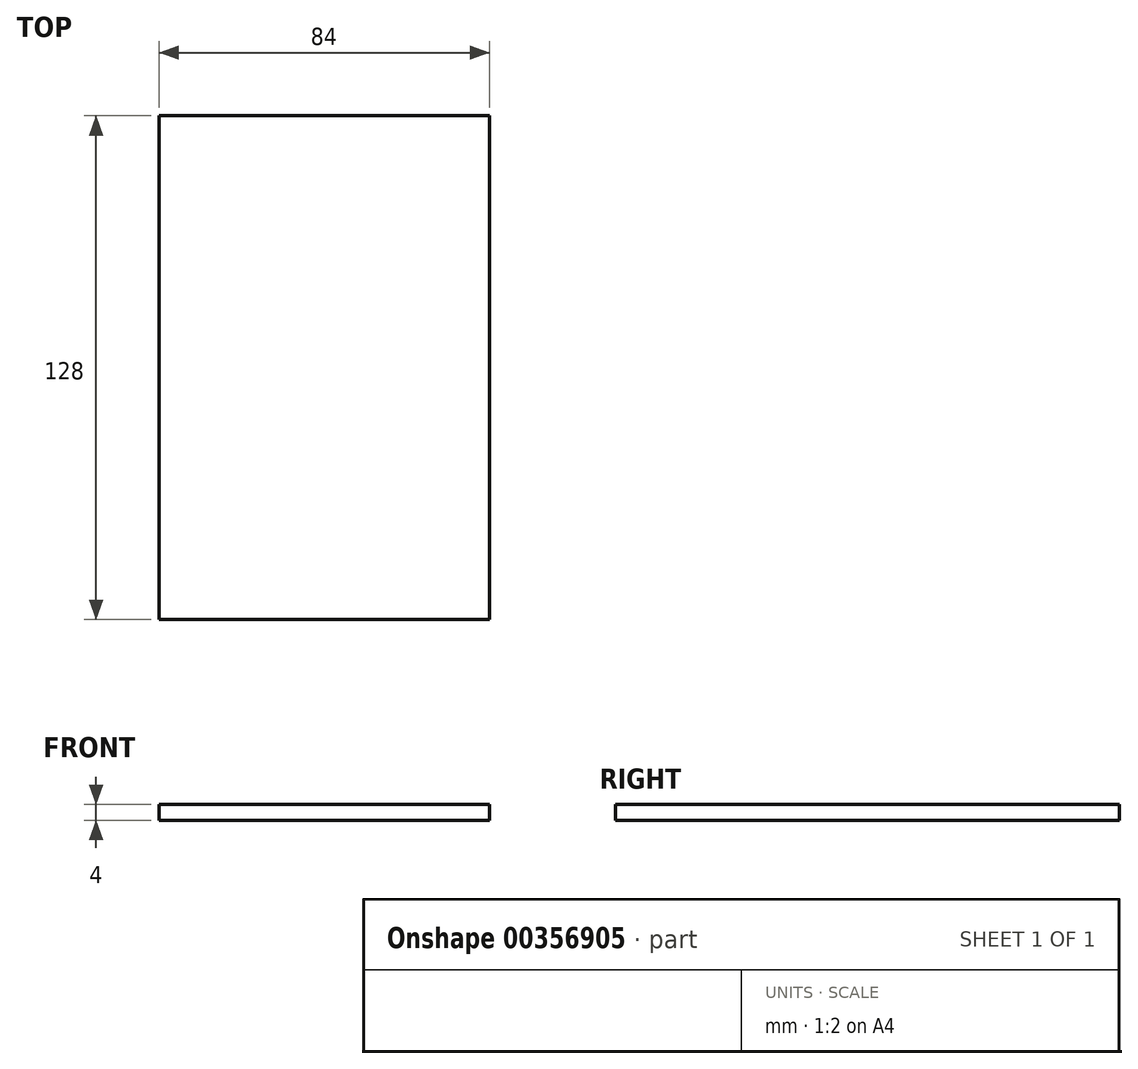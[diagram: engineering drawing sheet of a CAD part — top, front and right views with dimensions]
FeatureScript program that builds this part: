
annotation { "Feature Type Name" : "Feature", "Feature Type Description" : "" }
export const myFeature = defineFeature(function(context is Context, id is Id, definition is map)
    precondition{}
    {
        {
            var Q0;
            Q0=qCreatedBy(makeId("Top.planeOp"),FACE);
            var sketch = newSketch(context, id + "F0", { "sketchPlane" : qUnion([Q0])});
            skLineSegment(sketch, "E0.bottom", {"start": v(-42, 64) * mm, "end": v(42, 64) * mm});
            skLineSegment(sketch, "E0.top", {"start": v(-42, -64) * mm, "end": v(42, -64) * mm});
            skLineSegment(sketch, "E0.left", {"start": v(-42, 64) * mm, "end": v(-42, -64) * mm});
            skLineSegment(sketch, "E0.right", {"start": v(42, 64) * mm, "end": v(42, -64) * mm});
            skPoint(sketch, "E0.middle", {"position": v(0, 0) * mm});
            skSolve(sketch);
        }
        {
            var Q0;
            Q0=qSketchRegion(id+"F0",true);
            extrude(context, id + "F1", {"entities" : qUnion([Q0]), "depth" : 4 * mm});
        }
    });
